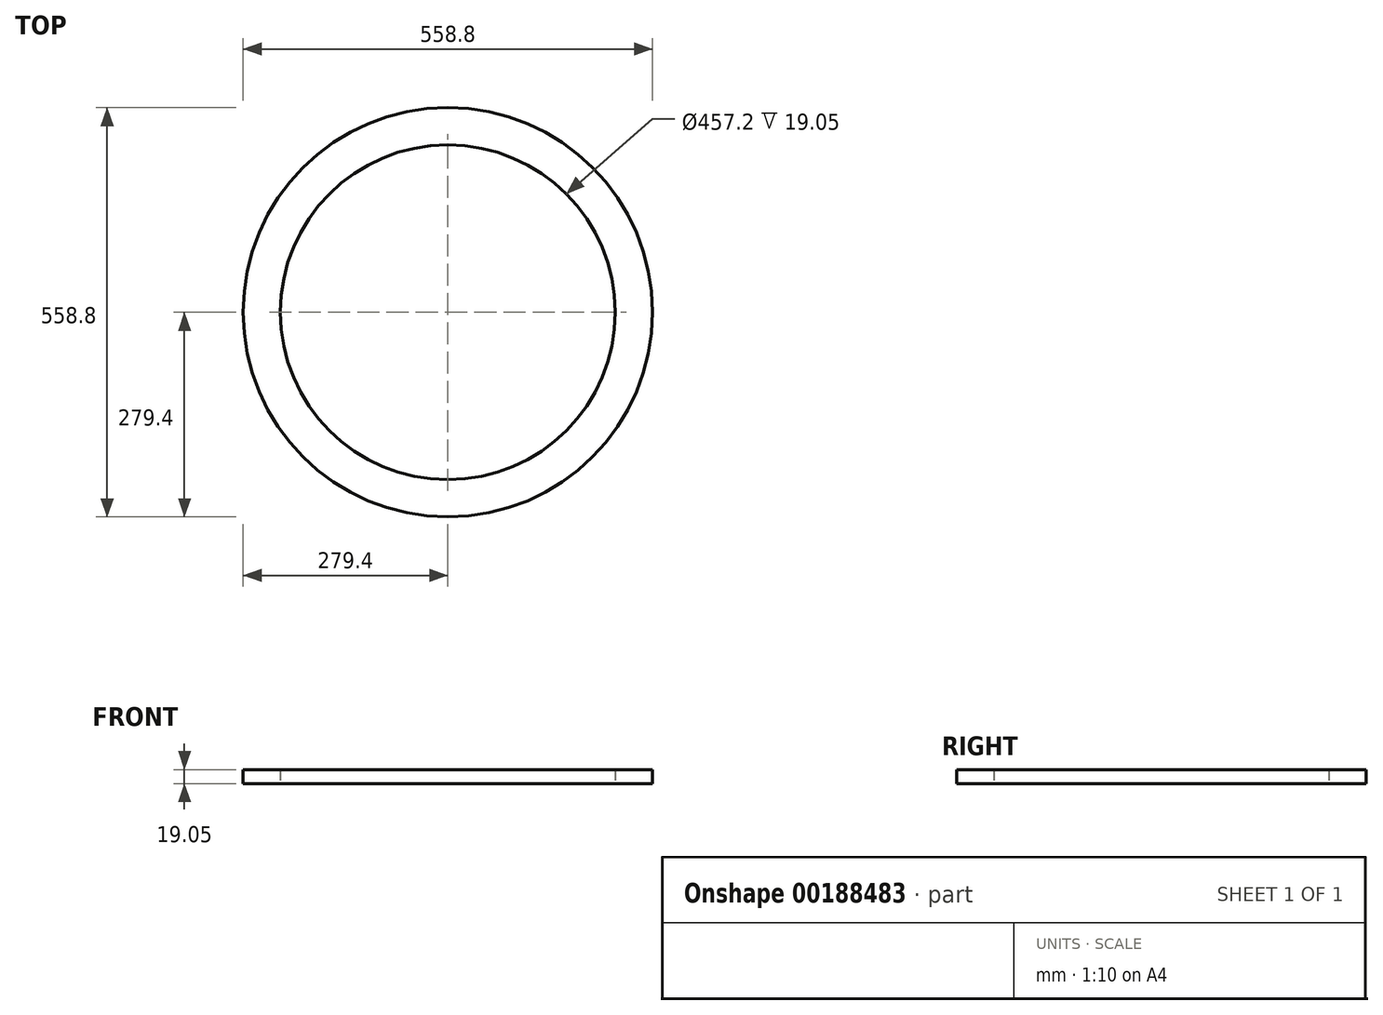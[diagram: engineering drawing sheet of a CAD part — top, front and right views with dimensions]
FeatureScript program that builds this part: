
annotation { "Feature Type Name" : "Feature", "Feature Type Description" : "" }
export const myFeature = defineFeature(function(context is Context, id is Id, definition is map)
    precondition{}
    {
        {
            var Q0;
            Q0=qCreatedBy(makeId("Top.planeOp"),FACE);
            var sketch = newSketch(context, id + "F0", { "sketchPlane" : qUnion([Q0])});
            skCircle(sketch, "E0", {"center": v(0, 0) * mm, "radius": 279.4 * mm});
            skCircle(sketch, "E1", {"center": v(0, 0) * mm, "radius": 228.6 * mm});
            skSolve(sketch);
        }
        {
            var Q0;
            Q0=makeQuery(id+"F0.imprint","IMPRINT",FACE,{"disambiguationData":[TD([[makeQuery(id+"F0.imprint","IMPRINT",EDGE,{"derivedFrom":sQuery(id+"F0.wireOp",EDGE,"E0")}),1.0]])]});
            extrude(context, id + "F1", {"entities" : qUnion([Q0]), "depth" : 19.05 * mm});
        }
    });
